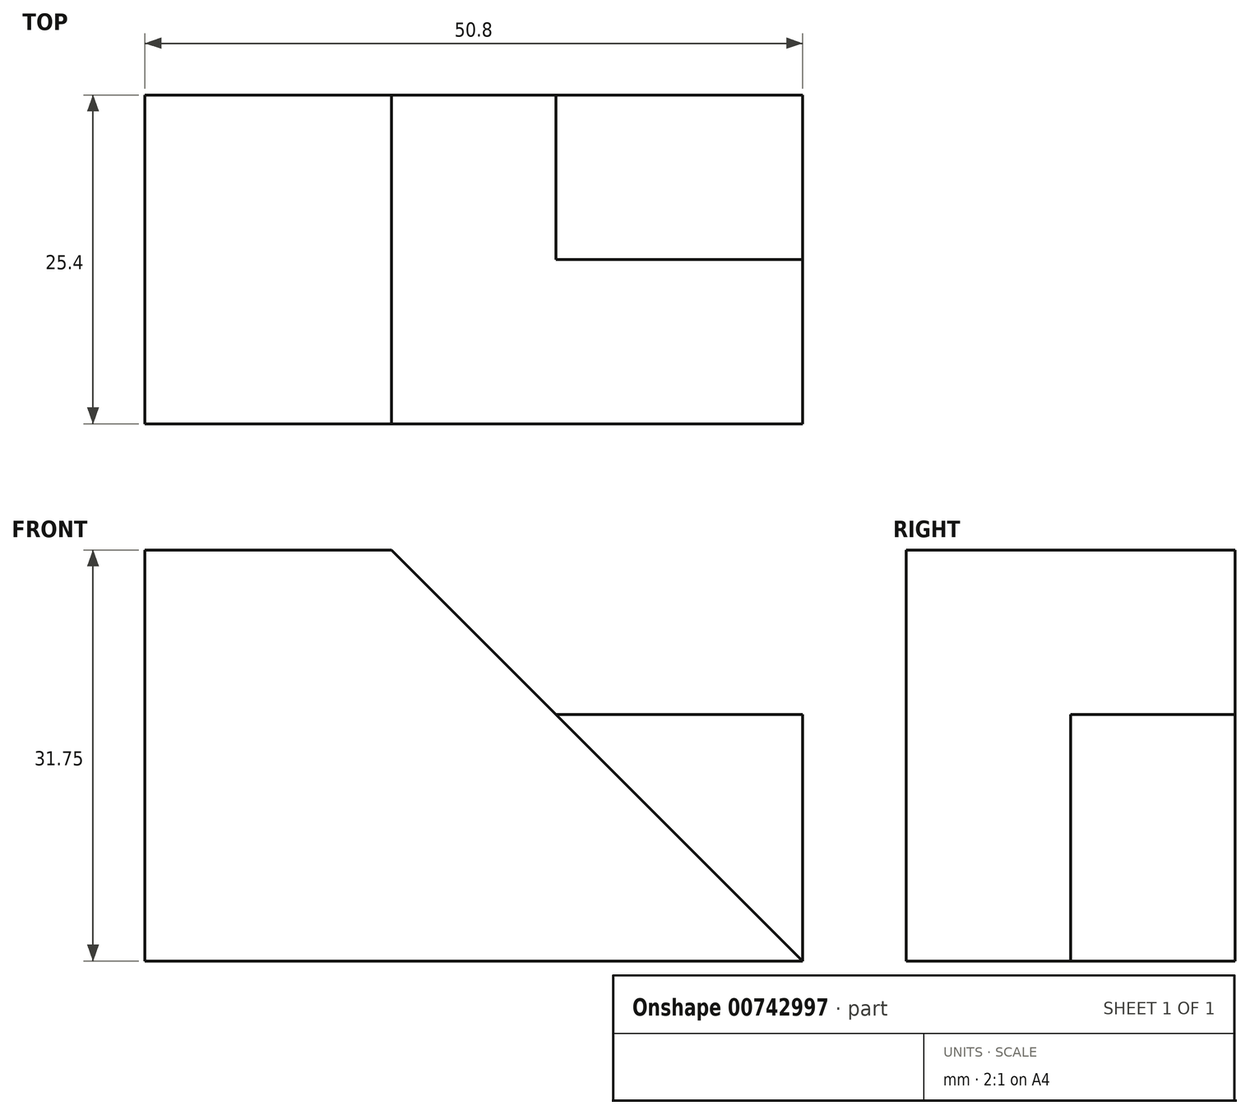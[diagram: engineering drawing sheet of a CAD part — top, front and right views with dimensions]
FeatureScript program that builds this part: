
annotation { "Feature Type Name" : "Feature", "Feature Type Description" : "" }
export const myFeature = defineFeature(function(context is Context, id is Id, definition is map)
    precondition{}
    {
        {
            var Q0;
            Q0=qCreatedBy(makeId("Front.planeOp"),FACE);
            var sketch = newSketch(context, id + "F0", { "sketchPlane" : qUnion([Q0])});
            skLineSegment(sketch, "E0", {"start": v(0, 0) * mm, "end": v(50.8, 0) * mm});
            skLineSegment(sketch, "E1", {"start": v(50.8, 0) * mm, "end": v(50.8, 31.75) * mm});
            skLineSegment(sketch, "E2", {"start": v(50.8, 31.75) * mm, "end": v(0, 31.75) * mm});
            skLineSegment(sketch, "E3", {"start": v(0, 31.75) * mm, "end": v(0, 0) * mm});
            skSolve(sketch);
        }
        {
            var Q0;
            Q0=makeQuery(id+"F0.imprint","IMPRINT",FACE,{"disambiguationData":[TD([[makeQuery(id+"F0.imprint","IMPRINT",EDGE,{"derivedFrom":sQuery(id+"F0.wireOp",EDGE,"E0")}),1.0]])]});
            extrude(context, id + "F1", {"entities" : qUnion([Q0]), "depth" : 25.4 * mm, "offsetDistance" : 25.4 * mm});
        }
        {
            var Q0;
            Q0=makeQuery(id+"F1.opExtrude","CAP_FACE",FACE,{"disambiguationData":[OSD([sQuery(id+"F0.wireOp",EDGE,"E0"),sQuery(id+"F0.wireOp",EDGE,"E1"),sQuery(id+"F0.wireOp",EDGE,"E2"),sQuery(id+"F0.wireOp",EDGE,"E3")])],"isStart":false});
            var sketch = newSketch(context, id + "F2", { "sketchPlane" : qUnion([Q0])});
            skLineSegment(sketch, "E4", {"start": v(19.05, 31.75) * mm, "end": v(50.8, 0) * mm});
            skSolve(sketch);
        }
        {
            var Q0;
            {var subQ0=sQuery(id+"F2.wireOp",EDGE,"E4");Q0=makeQuery(id+"F2.imprint","IMPRINT",FACE,{"disambiguationData":[TD([[makeQuery(id+"F2.imprint","IMPRINT",EDGE,{"derivedFrom":subQ0}),1.0]])]});}
            extrude(context, id + "F3", {"entities" : qUnion([Q0]), "operationType" : NewBodyOperationType.REMOVE, "oppositeDirection" : true, "depth" : 12.7 * mm, "offsetDistance" : 25.4 * mm});
        }
        {
            var Q0;
            Q0=makeQuery(id+"F3.boolean.opBoolean","COPY",FACE,{"derivedFrom":makeQuery(id+"F3.opExtrude","CAP_FACE",FACE,{"disambiguationData":[OSD([sQuery(id+"F0.wireOp",EDGE,"E1"),sQuery(id+"F0.wireOp",EDGE,"E2"),sQuery(id+"F2.wireOp",EDGE,"E4")])],"isStart":false})});
            var sketch = newSketch(context, id + "F4", { "sketchPlane" : qUnion([Q0])});
            skLineSegment(sketch, "E5", {"start": v(31.75, 19.05) * mm, "end": v(50.8, 19.05) * mm});
            skLineSegment(sketch, "E6", {"start": v(50.8, 19.05) * mm, "end": v(50.8, 31.75) * mm});
            skLineSegment(sketch, "E7", {"start": v(50.8, 31.75) * mm, "end": v(19.05, 31.75) * mm});
            skLineSegment(sketch, "E8", {"start": v(19.05, 31.75) * mm, "end": v(31.75, 19.05) * mm});
            skSolve(sketch);
        }
        {
            var Q0;
            Q0 = qSketchRegion(id + "F4", true);
            var Q1;
            Q1=makeQuery(id+"F4.imprint","IMPRINT",FACE,{"disambiguationData":[TD([[makeQuery(id+"F4.imprint","IMPRINT",EDGE,{"derivedFrom":sQuery(id+"F4.wireOp",EDGE,"E5")}),1.0]])]});
            extrude(context, id + "F5", {"entities" : qUnion([Q0, Q1]), "operationType" : NewBodyOperationType.REMOVE, "oppositeDirection" : true, "depth" : 25.4 * mm, "offsetDistance" : 25.4 * mm});
        }
    });
